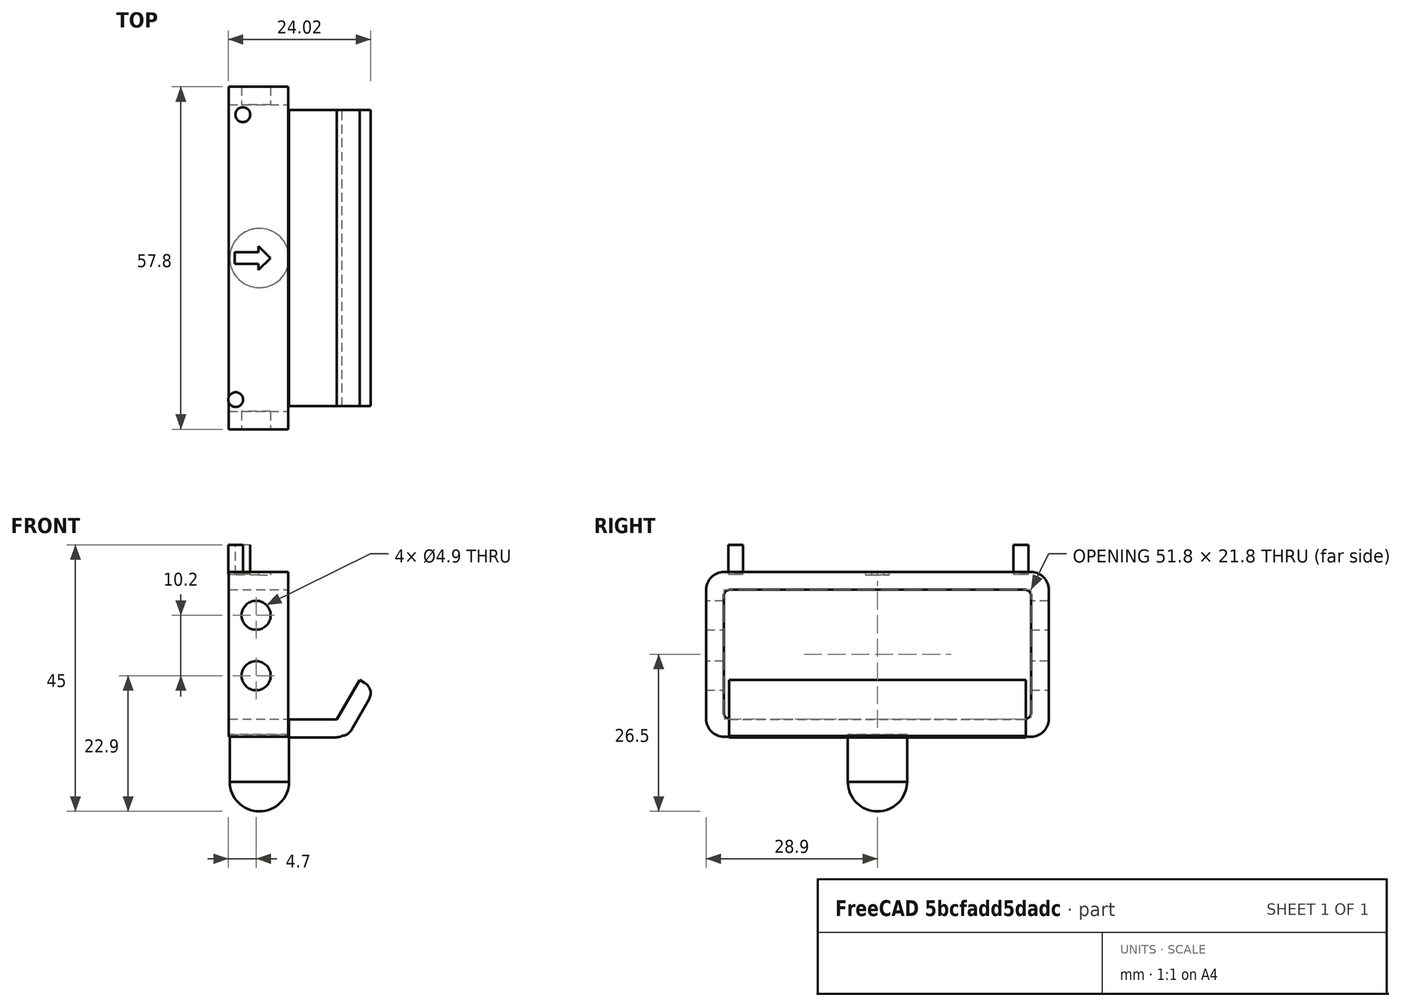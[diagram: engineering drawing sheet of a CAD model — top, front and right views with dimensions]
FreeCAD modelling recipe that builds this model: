
FCSTD DOCUMENT  (FreeCAD 0.17R13541 (Git))
Label: icelobot_b
License: All rights reserved
LicenseURL: http://en.wikipedia.org/wiki/All_rights_reserved
objects: Part::Cylinder×3, Part::Box×3, Part::Fillet×2, Part::Feature×1, Part::MultiFuse×1, Part::Sphere×1, Part::Cut×1
note: 12 computed .brp shape members not serialized (recipe doc carries the construction recipe); baked Part::Feature solids carry a one-line shape summary decoded from their .brp

FEATURE [Part::Feature] Part__Feature  label="back"
  Placement = pos=(10.3,-35,-45) rot=(0,1,0;1.5708rad)
  shape: bbox 10 x 57.8 x 27.8 mm, 30 faces (baked)
FEATURE [Part::Cylinder] Cylinder  label="Cilindrob1"
  Angle = 360
  AttacherType = Attacher::AttachEngine3D
  Height = 5
  Placement = pos=(12.2,-10.8,-33) rot=(0,0,1;0rad)
  Radius = 1.25
FEATURE [Part::Cylinder] Cylinder001  label="Cilindrob2"
  Angle = 360
  AttacherType = Attacher::AttachEngine3D
  Height = 5
  Placement = pos=(11,-58.9,-33) rot=(0,0,1;0rad)
  Radius = 1.25
FEATURE [Part::Box] Box  label="Cubo"
  AttacherType = Attacher::AttachEngine3D
  Height = 3
  Length = 10
  Placement = pos=(30,-60,-60.5) rot=(0,-1,0;1.0472rad)
  Width = 50
FEATURE [Part::Box] Box001  label="Cubo001"
  AttacherType = Attacher::AttachEngine3D
  Height = 3
  Length = 10
  Placement = pos=(20,-60,-60.5) rot=(0,0,1;0rad)
  Width = 50
FEATURE [Part::Fillet] Fillet
  Base = -> Box
  Edges = 2 edges r=2: [Edge4,Edge8]
  Placement = pos=(-0.5,0,-0.5) rot=(0,0,1;0rad)
FEATURE [Part::Fillet] Fillet001
  Base = -> Box001
  Edges = 1 edges r=2: [Edge8]
FEATURE [Part::MultiFuse] Fusion  label="SoportePila"
  Shapes = -> [Fillet,Fillet001]
FEATURE [Part::Sphere] Sphere  label="Esfera"
  Angle1 = -90
  Angle2 = 90
  Angle3 = 360
  AttacherType = Attacher::AttachEngine3D
  Radius = 5
FEATURE [Part::Box] Box002  label="Cubo002"
  AttacherType = Attacher::AttachEngine3D
  Height = 10
  Length = 10
  Placement = pos=(-5,-5,0) rot=(0,0,1;0rad)
  Width = 10
FEATURE [Part::Cut] Cut
  Base = -> Sphere
  Placement = pos=(15,-35,-68) rot=(0,0,1;0rad)
  Tool = -> Box002
FEATURE [Part::Cylinder] Cylinder002  label="Cilindro"
  Angle = 360
  AttacherType = Attacher::AttachEngine3D
  Height = 8
  Placement = pos=(15,-35,-68) rot=(0,0,1;0rad)
  Radius = 5
